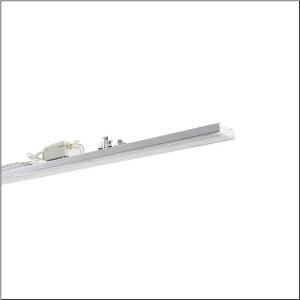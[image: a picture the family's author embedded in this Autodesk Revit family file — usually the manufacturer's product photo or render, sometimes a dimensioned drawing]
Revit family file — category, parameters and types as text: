
# Revit family: licross_11_recessed_ho_51tl12cn46xm
name_source: partatom
category: Lighting Fixtures
units: mm (PartAtom-declared; Revit-internal decimal feet)

## family parameters
Cut with Voids When Loaded = No
Host = Face
Light Source = No
Part Type = Normal
Room Calculation Point = No
Round Connector Dimension = Use Diameter
Shared = No

## types (1)
- --- (1 x LED, 6020 lm, 30.1 W, 4000K)
    Apparent Load = 30 VA
    CIE Flux Codes = 66 91 98 100 100
    Color Rendering = 80
    Color Temperature = 4000K
    Default Elevation = 1800 mm
    Description = Licross 11 Recessed HO, luminaire insert, of sheet steel, coil coated, white, length: 1.500mm, width: 66mm, height: 67mm, LED rated luminous flux: 6.020lm, light colour: 840, SDCM (Standard Deviation of Colour Matching)MacAdam ≤ 2 SDCM (initial), control gear: ON/OFF Multilumen, CLOi, with plug, 3-pole, with phase selection, mains connection: 220..240V, AC, 50/60Hz, start of lifetime: 30W, end of service life: 33W, internal wiring halogen-free, primary optical cover: cover, of PMMA, light emission: direct distribution, primary light characteristic: symmetric, protection rating (complete): IP40, insulation class (complete): insulation class I (protective earthing), certification: CE, ENEC, VDE, UKCA, protection symbol: D if used in an environment without relevant dust loads with corresponding accessories, impact resistance: IK06, permissible ambient temperature for indoor applications: -35..+50°C, corresponds to IFS (International Featured Standards) requirements for safety and quality in the food industry, reducing of maximum allowable ambient temperature of 5°C with ceiling mounting, LABS conformity tested according to VDMA 24364:2018-05, The light source and the operating device comply with the requirements of the Ecodesign Regulation (EU) 2019/2020 and are replaceable in accordance with this regulation, packaging unit: 1 piece
    Height = 58 mm
    Lamp = 1 x LED
    Lamp Light Flux = 6020 lm
    Lamp Power = 30.1 W
    Lamp count = 1
    Length = 1500 mm
    Luminous efficacy = 200 lm/W
    Manufacturer = Siteco
    ModVariant = No
    Model = 51TL12CN46XM
    Mounting Place = Ceiling
    Mounting Type = Pendant
    Number of Poles = 1
    OnlyDefault = Yes
    Power Factor = 1
    Product Name = Licross 11 Recessed HO
    Product group = luminaire insert | ceiling pendant
    ProductGroupID = 901
    Protection Class = Protection class I
    Protection Degree = IP 40
    RLX_Detail_Level = 1
    RLX_Emergency_Light_Flux = 0 lm
    RLX_Emergency_Type = 0
    RLX_Emergency_Type_DB = No
    RlxData = <blob elided: 22477 chars, md5=b578b7c4>
    Socket = socket
    Standby Power = 0 W
    System Light Flux = 6020 lm
    System Power = 30 W
    Type Comments = factory setting: luminous flux: 100 % | (A | C | E) | 71 mA
    Type Image = l_1296930.jpg
    URL = http://relux.com
    VarID = @adj_000305
    Voltage = 0 V
    Weight = 0.00 kg
    Width = 66 mm

## geometry (parser evidence)
native form markers: Blend x4, Sweep x11
no freeform markers — native parametric forms only
